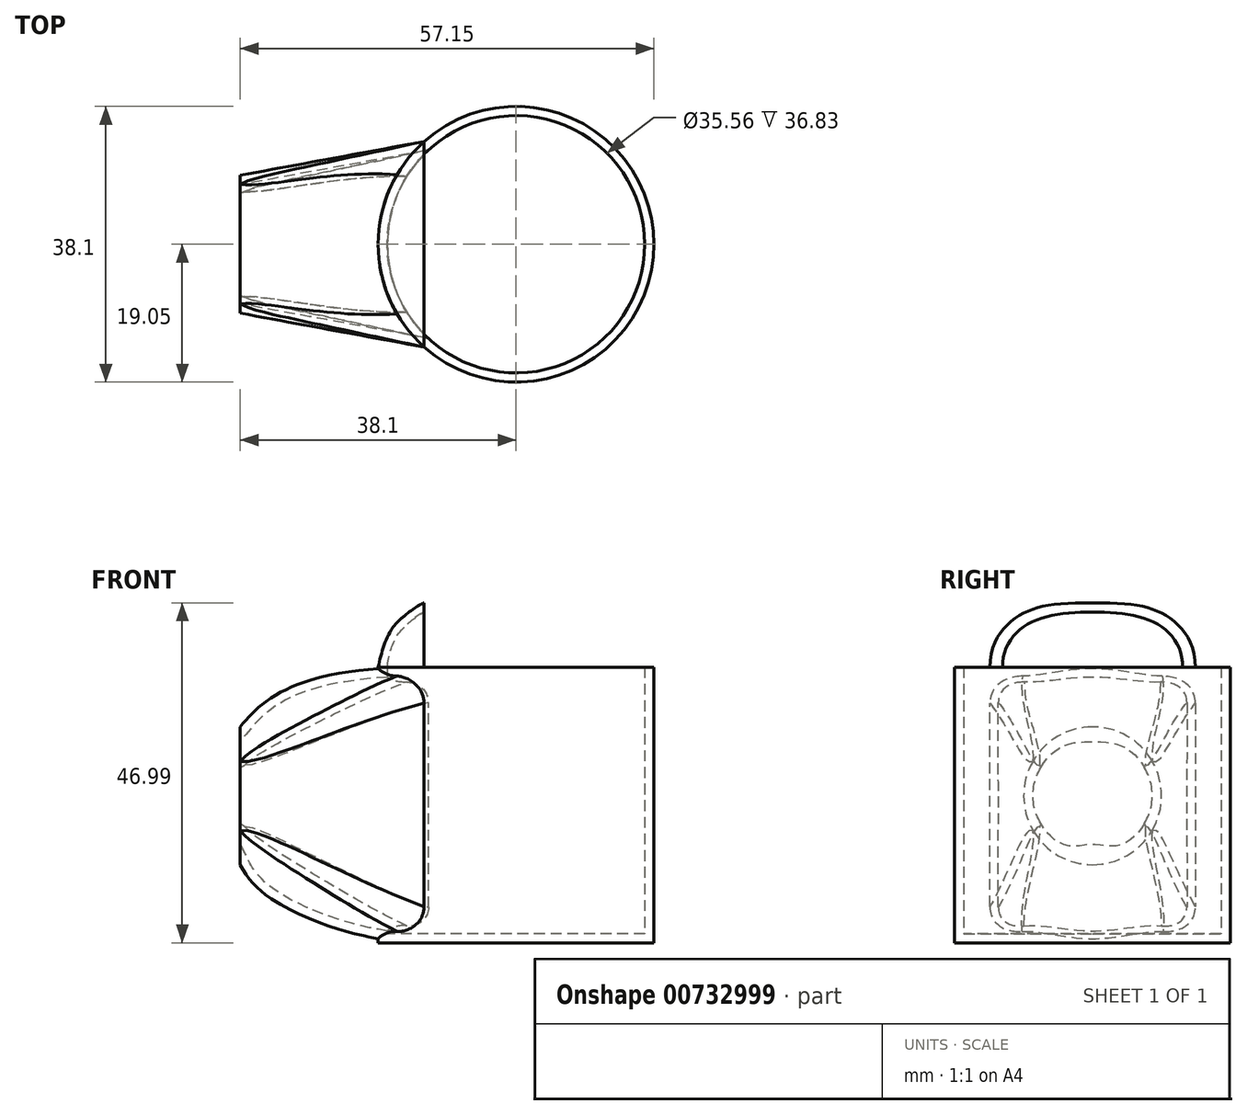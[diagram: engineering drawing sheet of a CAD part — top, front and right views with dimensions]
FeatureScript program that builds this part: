
annotation { "Feature Type Name" : "Feature", "Feature Type Description" : "" }
export const myFeature = defineFeature(function(context is Context, id is Id, definition is map)
    precondition{}
    {
        {
            var Q0;
            Q0=qCreatedBy(makeId("Right.planeOp"),FACE);
            cPlane(context, id + "F0", {"entities" : qUnion([Q0]), "cplaneType" : CPlaneType.OFFSET, "offset" : 12.7 * mm, "oppositeDirection" : true, "width" : 152.4 * mm, "height" : 152.4 * mm});
        }
        {
            var Q0;
            Q0=qCreatedBy(makeId("Top.planeOp"),FACE);
            var sketch = newSketch(context, id + "F1", { "sketchPlane" : qUnion([Q0])});
            skCircle(sketch, "E0", {"center": v(0, 0) * mm, "radius": 19.05 * mm});
            skSolve(sketch);
        }
        {
            var Q0;
            Q0=makeQuery(id+"F1.imprint","IMPRINT",FACE,{"disambiguationData":[TD([[makeQuery(id+"F1.imprint","IMPRINT",EDGE,{"derivedFrom":sQuery(id+"F1.wireOp",EDGE,"E0")}),1.0]])]});
            extrude(context, id + "F2", {"entities" : qUnion([Q0]), "depth" : 38.1 * mm, "offsetDistance" : 25.4 * mm});
        }
        {
            var Q0;
            Q0=qCreatedBy(id+"F0.planeOp",FACE);
            var sketch = newSketch(context, id + "F3", { "sketchPlane" : qUnion([Q0])});
            skLineSegment(sketch, "E1", {"start": v(14.2, 38.1) * mm, "end": v(14.2, 0) * mm});
            skLineSegment(sketch, "E2", {"start": v(-14.2, 0) * mm, "end": v(-14.2, 38.1) * mm});
            skLineSegment(sketch, "E3", {"start": v(14.2, 38.1) * mm, "end": v(-14.2, 38.1) * mm});
            skLineSegment(sketch, "E4", {"start": v(14.2, 0) * mm, "end": v(-14.2, 0) * mm});
            skLineSegment(sketch, "E5", {"start": v(0, 38.1) * mm, "end": v(0, 0) * mm, "construction": true});
            skSolve(sketch);
        }
        {
            var Q0;
            Q0=qCreatedBy(makeId("Right.planeOp"),FACE);
            cPlane(context, id + "F4", {"entities" : qUnion([Q0]), "cplaneType" : CPlaneType.OFFSET, "offset" : 38.1 * mm, "oppositeDirection" : true, "width" : 152.4 * mm, "height" : 152.4 * mm});
        }
        {
            var Q0;
            Q0=qCreatedBy(id+"F4.planeOp",FACE);
            var sketch = newSketch(context, id + "F5", { "sketchPlane" : qUnion([Q0])});
            skCircle(sketch, "E6", {"center": v(0, 20.32) * mm, "radius": 9.53 * mm});
            skLineSegment(sketch, "E7", {"start": v(0, 29.85) * mm, "end": v(0, 10.8) * mm, "construction": true});
            skSolve(sketch);
        }
        {
            var Q0;
            Q0=qCreatedBy(makeId("Front.planeOp"),FACE);
            var sketch = newSketch(context, id + "F6", { "sketchPlane" : qUnion([Q0])});
            skFitSpline(sketch, "E8", {"points": [v(-12.7, 0) * mm, v(-32.84, 5.48) * mm, v(-38.1, 10.8) * mm], "startDerivative": vector(-36.99, 0) * mm, "endDerivative": vector(-8.36, 16.5) * mm});
            skFitSpline(sketch, "E9", {"points": [v(-12.7, 38.1) * mm, v(-31.4, 35.17) * mm, v(-38.1, 29.85) * mm], "startDerivative": vector(-41.86, 0) * mm, "endDerivative": vector(-13.07, -16.64) * mm});
            skSolve(sketch);
        }
        {
            var Q1;
            Q1=makeQuery(id+"F3.imprint","IMPRINT",FACE,{"disambiguationData":[TD([[makeQuery(id+"F3.imprint","IMPRINT",EDGE,{"derivedFrom":sQuery(id+"F3.wireOp",EDGE,"E1")}),-1.0]])]});
            var Q2;
            Q2=makeQuery(id+"F5.imprint","IMPRINT",FACE,{"disambiguationData":[TD([[makeQuery(id+"F5.imprint","IMPRINT",EDGE,{"derivedFrom":sQuery(id+"F5.wireOp",EDGE,"E6")}),1.0]])]});
            var Q3;
            Q3=sQuery(id+"F6.wireOp",EDGE,"E9");
            var Q4;
            Q4=sQuery(id+"F6.wireOp",EDGE,"E8");
            loft(context, id + "F7", {"operationType" : NewBodyOperationType.ADD, "addGuides" : true, "sheetProfilesArray" : [{ "sheetProfileEntities" : qUnion([Q1]) }, { "sheetProfileEntities" : qUnion([Q2]) }], "guidesArray" : [{ "guideEntities" : qUnion([Q3]), "guideDerivativeType" : LoftGuideDerivativeType.DEFAULT, "guideDerivativeMagnitude" : 1 }, { "guideEntities" : qUnion([Q4]), "guideDerivativeType" : LoftGuideDerivativeType.DEFAULT, "guideDerivativeMagnitude" : 1 }]});
        }
        {
            var Q0;
            Q0=makeQuery(id+"F7.opLoft","SWEPT_EDGE",EDGE,{"disambiguationData":[OSD([sQuery(id+"F3.wireOp",EDGE,"E1"),sQuery(id+"F3.wireOp",EDGE,"E3"),sQuery(id+"F3.wireOp",EDGE,"E4"),sQuery(id+"F5.wireOp",EDGE,"E6")])]});
            var Q1;
            Q1=makeQuery(id+"F7.opLoft","SWEPT_EDGE",EDGE,{"disambiguationData":[OSD([sQuery(id+"F3.wireOp",EDGE,"E1"),sQuery(id+"F3.wireOp",EDGE,"E3"),sQuery(id+"F5.wireOp",EDGE,"E6"),sQuery(id+"F6.wireOp",EDGE,"E9")])]});
            var Q2;
            Q2=makeQuery(id+"F7.opLoft","SWEPT_EDGE",EDGE,{"disambiguationData":[OSD([sQuery(id+"F3.wireOp",EDGE,"E2"),sQuery(id+"F3.wireOp",EDGE,"E3"),sQuery(id+"F3.wireOp",EDGE,"E4"),sQuery(id+"F5.wireOp",EDGE,"E6")])]});
            var Q3;
            Q3=makeQuery(id+"F7.opLoft","SWEPT_EDGE",EDGE,{"disambiguationData":[OSD([sQuery(id+"F3.wireOp",EDGE,"E2"),sQuery(id+"F3.wireOp",EDGE,"E4"),sQuery(id+"F5.wireOp",EDGE,"E6"),sQuery(id+"F6.wireOp",EDGE,"E8")])]});
            fillet(context, id + "F8", {"entities" : qUnion([Q0, Q1, Q2, Q3]), "radius" : 5.08 * mm, "tangentPropagation" : true, "allowEdgeOverflow" : false});
        }
        {
            var Q0;
            Q0=makeQuery(id+"F2.opExtrude","CAP_FACE",FACE,{"disambiguationData":[OSD([sQuery(id+"F1.wireOp",EDGE,"E0")])],"isStart":false});
            var Q1;
            Q1=makeQuery(id+"F7.opLoft","CAP_FACE",FACE,{"disambiguationData":[OSD([makeQuery(id+"F5.imprint","IMPRINT",FACE,{"disambiguationData":[TD([[makeQuery(id+"F5.imprint","IMPRINT",EDGE,{"derivedFrom":sQuery(id+"F5.wireOp",EDGE,"E6")}),1.0]])]})])],"isStart":true});
            shell(context, id + "F9", {"entities" : qUnion([Q0, Q1]), "thickness" : 1.27 * mm});
        }
        {
            var Q0;
            Q0=qCreatedBy(makeId("Top.planeOp"),FACE);
            cPlane(context, id + "F10", {"entities" : qUnion([Q0]), "cplaneType" : CPlaneType.OFFSET, "offset" : 38.1 * mm, "width" : 152.4 * mm, "height" : 152.4 * mm});
        }
        {
            var Q0;
            Q0=qCreatedBy(id+"F10.planeOp",FACE);
            var sketch = newSketch(context, id + "F11", { "sketchPlane" : qUnion([Q0])});
            skLineSegment(sketch, "E10", {"start": v(-12.7, -14.2) * mm, "end": v(-12.7, 14.2) * mm});
            skArc(sketch, "E11.0", {"start": v(-12.7, 14.2) * mm, "mid": v(-19.05, 0) * mm, "end": v(-12.7, -14.2) * mm});
            skSolve(sketch);
        }
        {
            var Q0;
            Q0=qCreatedBy(id+"F0.planeOp",FACE);
            var sketch = newSketch(context, id + "F12", { "sketchPlane" : qUnion([Q0])});
            skLineSegment(sketch, "E12", {"start": v(0, 38.1) * mm, "end": v(0, 47) * mm, "construction": true});
            skFitSpline(sketch, "E13", {"points": [v(14.2, 38.1) * mm, v(10.27, 45.13) * mm, v(0, 47) * mm], "startDerivative": vector(0, 22.55) * mm, "endDerivative": vector(-29.52, 0) * mm});
            skFitSpline(sketch, "E14.MirrorCS", {"points": [v(-14.2, 38.1) * mm, v(-10.27, 45.13) * mm, v(0, 47) * mm], "startDerivative": vector(0, 22.55) * mm, "endDerivative": vector(29.52, 0) * mm});
            skSolve(sketch);
        }
        {
            var Q0;
            Q0=qCreatedBy(makeId("Front.planeOp"),FACE);
            var sketch = newSketch(context, id + "F13", { "sketchPlane" : qUnion([Q0])});
            skFitSpline(sketch, "E15", {"points": [v(-12.7, 47) * mm, v(-16.95, 43.64) * mm, v(-19.05, 38.1) * mm], "startDerivative": vector(-14.23, -8.48) * mm, "endDerivative": vector(-3.66, -16.93) * mm});
            skSolve(sketch);
        }
        {
            var Q1;
            Q1=makeQuery(id+"F11.imprint","IMPRINT",FACE,{"disambiguationData":[TD([[makeQuery(id+"F11.imprint","IMPRINT",EDGE,{"derivedFrom":sQuery(id+"F11.wireOp",EDGE,"E10")}),1.0]])]});
            var Q2;
            Q2=sQuery(id+"F12.wireOp",VERTEX,"E12.end");
            var Q3;
            Q3=makeQuery(id+"F11.imprint","IMPRINT",FACE,{"disambiguationData":[TD([[makeQuery(id+"F11.imprint","IMPRINT",EDGE,{"derivedFrom":sQuery(id+"F11.wireOp",EDGE,"E10")}),1.0]])]});
            var Q4;
            Q4=sQuery(id+"F12.wireOp",VERTEX,"E12.end");
            var Q5;
            Q5=sQuery(id+"F13.wireOp",EDGE,"E15");
            var Q6;
            Q6=sQuery(id+"F12.wireOp",EDGE,"E13");
            var Q7;
            Q7=sQuery(id+"F12.wireOp",EDGE,"E14.MirrorCS");
            loft(context, id + "F14", {"addGuides" : true, "sheetProfilesArray" : [{ "sheetProfileEntities" : qUnion([Q1]) }, { "sheetProfileEntities" : qUnion([Q2]) }], "wireProfilesArray" : [{ "wireProfileEntities" : qUnion([Q3]) }, { "wireProfileEntities" : qUnion([Q4]) }], "guidesArray" : [{ "guideEntities" : qUnion([Q5]), "guideDerivativeType" : LoftGuideDerivativeType.DEFAULT, "guideDerivativeMagnitude" : 1 }, { "guideEntities" : qUnion([Q6]), "guideDerivativeType" : LoftGuideDerivativeType.DEFAULT, "guideDerivativeMagnitude" : 1 }, { "guideEntities" : qUnion([Q7]), "guideDerivativeType" : LoftGuideDerivativeType.DEFAULT, "guideDerivativeMagnitude" : 1 }]});
        }
        {
            var Q0;
            Q0=qCreatedBy(id+"F10.planeOp",FACE);
            var sketch = newSketch(context, id + "F15", { "sketchPlane" : qUnion([Q0])});
            skLineSegment(sketch, "E16", {"start": v(-12.7, 12.44) * mm, "end": v(-12.7, -12.44) * mm});
            skArc(sketch, "E17.0", {"start": v(-12.7, 12.44) * mm, "mid": v(-17.78, 0) * mm, "end": v(-12.7, -12.44) * mm});
            skSolve(sketch);
        }
        {
            var Q0;
            Q0=qCreatedBy(id+"F0.planeOp",FACE);
            var sketch = newSketch(context, id + "F16", { "sketchPlane" : qUnion([Q0])});
            skLineSegment(sketch, "E18", {"start": v(0, 45.72) * mm, "end": v(0, 38.1) * mm, "construction": true});
            skFitSpline(sketch, "E19", {"points": [v(12.44, 38.1) * mm, v(9.3, 43.84) * mm, v(0, 45.72) * mm], "startDerivative": vector(0, 16.26) * mm, "endDerivative": vector(-19.06, 0) * mm});
            skFitSpline(sketch, "E20.MirrorCS", {"points": [v(-12.44, 38.1) * mm, v(-9.3, 43.84) * mm, v(0, 45.72) * mm], "startDerivative": vector(0, 16.26) * mm, "endDerivative": vector(19.06, 0) * mm});
            skSolve(sketch);
        }
        {
            var Q0;
            Q0=qCreatedBy(makeId("Front.planeOp"),FACE);
            var sketch = newSketch(context, id + "F17", { "sketchPlane" : qUnion([Q0])});
            skFitSpline(sketch, "E21", {"points": [v(-12.7, 45.72) * mm, v(-16.27, 42.67) * mm, v(-17.78, 38.1) * mm], "startDerivative": vector(-5, -3.14) * mm, "endDerivative": vector(-0.65, -6.68) * mm});
            skSolve(sketch);
        }
        {
            var Q0;
            Q0=makeQuery(id+"F15.imprint","IMPRINT",FACE,{"disambiguationData":[TD([[makeQuery(id+"F15.imprint","IMPRINT",EDGE,{"derivedFrom":sQuery(id+"F15.wireOp",EDGE,"E16")}),-1.0]])]});
            var Q1;
            Q1=sQuery(id+"F16.wireOp",VERTEX,"E18.start");
            var Q2;
            Q2=sQuery(id+"F16.wireOp",EDGE,"E19");
            var Q3;
            Q3=sQuery(id+"F16.wireOp",EDGE,"E20.MirrorCS");
            var Q4;
            Q4=sQuery(id+"F17.wireOp",EDGE,"E21");
            loft(context, id + "F18", {"addGuides" : true, "sheetProfilesArray" : [{ "sheetProfileEntities" : qUnion([Q0]) }, { "sheetProfileEntities" : qUnion([Q1]) }], "guidesArray" : [{ "guideEntities" : qUnion([Q2]), "guideDerivativeType" : LoftGuideDerivativeType.DEFAULT, "guideDerivativeMagnitude" : 1 }, { "guideEntities" : qUnion([Q3]), "guideDerivativeType" : LoftGuideDerivativeType.DEFAULT, "guideDerivativeMagnitude" : 1 }, { "guideEntities" : qUnion([Q4]), "guideDerivativeType" : LoftGuideDerivativeType.DEFAULT, "guideDerivativeMagnitude" : 1 }]});
        }
        {
            var Q0;
            Q0=makeQuery(id+"F18.opLoft","SWEPT_BODY",BODY,{"disambiguationData":[OSD([makeQuery(id+"F15.imprint","IMPRINT",FACE,{"disambiguationData":[TD([[makeQuery(id+"F15.imprint","IMPRINT",EDGE,{"derivedFrom":sQuery(id+"F15.wireOp",EDGE,"E16")}),-1.0]])]}),sQuery(id+"F16.wireOp",VERTEX,"E18.start"),sQuery(id+"F16.wireOp",EDGE,"E19"),sQuery(id+"F16.wireOp",EDGE,"E20.MirrorCS"),sQuery(id+"F17.wireOp",EDGE,"E21")])]});
            var Q1;
            Q1=makeQuery(id+"F14.opLoft","SWEPT_BODY",BODY,{"disambiguationData":[OSD([makeQuery(id+"F11.imprint","IMPRINT",FACE,{"disambiguationData":[TD([[makeQuery(id+"F11.imprint","IMPRINT",EDGE,{"derivedFrom":sQuery(id+"F11.wireOp",EDGE,"E10")}),1.0]])]}),sQuery(id+"F12.wireOp",VERTEX,"E12.end"),sQuery(id+"F12.wireOp",EDGE,"E13"),sQuery(id+"F12.wireOp",EDGE,"E14.MirrorCS"),sQuery(id+"F13.wireOp",EDGE,"E15")])]});
            booleanBodies(context, id + "F19", {"operationType" : BooleanOperationType.SUBTRACTION, "tools" : qUnion([Q0]), "targets" : qUnion([Q1])});
        }
    });
